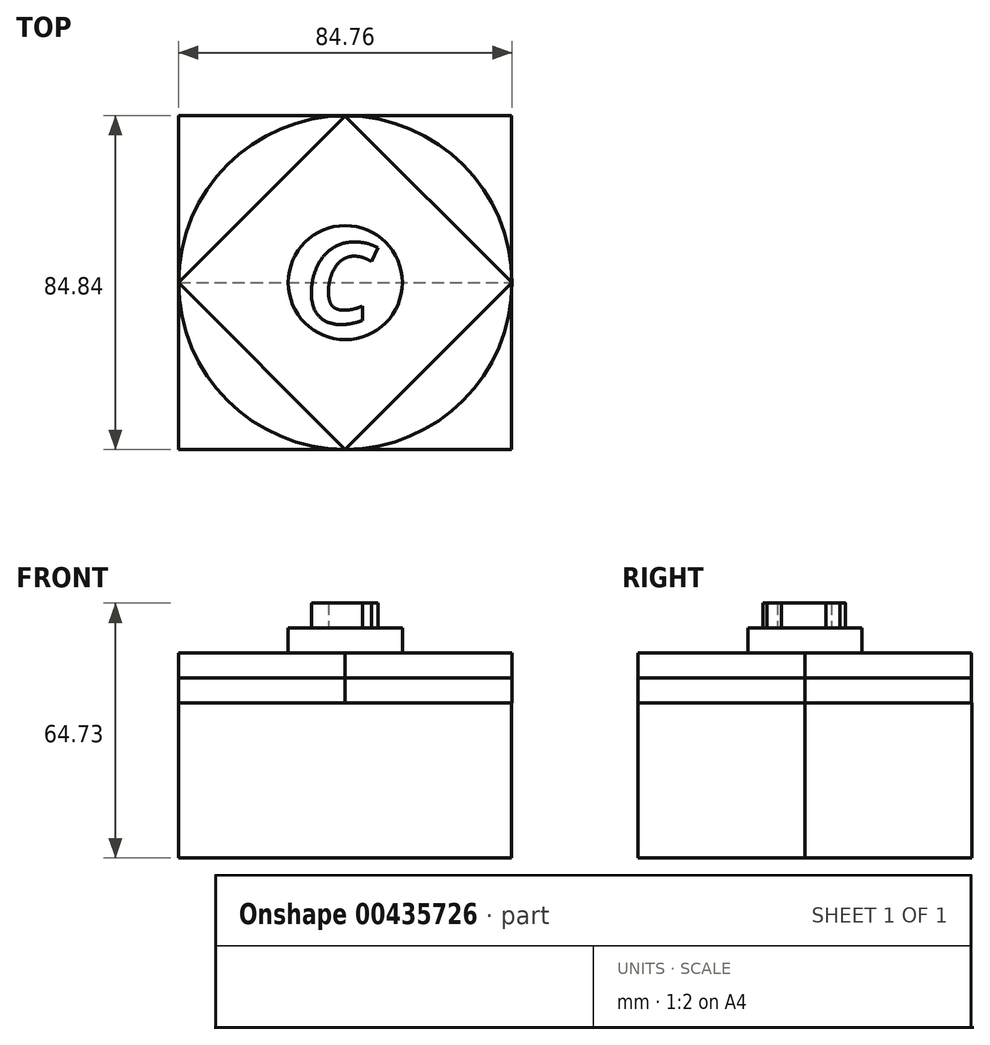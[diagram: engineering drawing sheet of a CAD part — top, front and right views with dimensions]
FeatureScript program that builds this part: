
annotation { "Feature Type Name" : "Feature", "Feature Type Description" : "" }
export const myFeature = defineFeature(function(context is Context, id is Id, definition is map)
    precondition{}
    {
        {
            var Q0;
            Q0=qCreatedBy(makeId("Top.planeOp"),FACE);
            var sketch = newSketch(context, id + "F0", { "sketchPlane" : qUnion([Q0])});
            skCircle(sketch, "E0", {"center": v(0, 0) * mm, "radius": 42.35 * mm});
            skLineSegment(sketch, "E1", {"start": v(0, 0) * mm, "end": v(0, 42.35) * mm});
            skLineSegment(sketch, "E2", {"start": v(0, 42.35) * mm, "end": v(-42.35, 0) * mm});
            skLineSegment(sketch, "E3", {"start": v(-42.35, 0) * mm, "end": v(0, -42.35) * mm});
            skLineSegment(sketch, "E4", {"start": v(0, -42.35) * mm, "end": v(42.35, 0) * mm});
            skLineSegment(sketch, "E5", {"start": v(42.35, 0) * mm, "end": v(0, 42.35) * mm});
            skLineSegment(sketch, "E6", {"start": v(0, 0) * mm, "end": v(42.35, 0) * mm});
            skLineSegment(sketch, "E7", {"start": v(0, 0) * mm, "end": v(0, -42.35) * mm});
            skLineSegment(sketch, "E8", {"start": v(0, 0) * mm, "end": v(-42.35, 0) * mm});
            skCircle(sketch, "E9", {"center": v(0, 0) * mm, "radius": 14.5 * mm});
            skText(sketch, "E10", { "text": "C", "fontName": "OpenSans-BoldItalic.ttf"});
            const initialGuessF0  = {"E10": [-0.01032, -0.01037, 1, 0, 0.02054]};
            skSetInitialGuess(sketch, initialGuessF0);
            skSolve(sketch);
        }
        {
            var Q0;
            {var subQ0=sQuery(id+"F0.wireOp",EDGE,"E2");Q0=makeQuery(id+"F0.imprint","IMPRINT",FACE,{"disambiguationData":[TD([[makeQuery(id+"F0.imprint","IMPRINT",EDGE,{"derivedFrom":subQ0}),-1.0]])]});}
            var Q1;
            {var subQ0=sQuery(id+"F0.wireOp",EDGE,"E5");Q1=makeQuery(id+"F0.imprint","IMPRINT",FACE,{"disambiguationData":[TD([[makeQuery(id+"F0.imprint","IMPRINT",EDGE,{"derivedFrom":subQ0}),-1.0]])]});}
            var Q2;
            {var subQ0=sQuery(id+"F0.wireOp",EDGE,"E4");Q2=makeQuery(id+"F0.imprint","IMPRINT",FACE,{"disambiguationData":[TD([[makeQuery(id+"F0.imprint","IMPRINT",EDGE,{"derivedFrom":subQ0}),-1.0]])]});}
            var Q3;
            {var subQ0=sQuery(id+"F0.wireOp",EDGE,"E3");Q3=makeQuery(id+"F0.imprint","IMPRINT",FACE,{"disambiguationData":[TD([[makeQuery(id+"F0.imprint","IMPRINT",EDGE,{"derivedFrom":subQ0}),-1.0]])]});}
            extrude(context, id + "F1", {"entities" : qUnion([Q0, Q1, Q2, Q3]), "depth" : 6.35 * mm});
        }
        {
            var Q0;
            {var subQ0=sQuery(id+"F0.wireOp",EDGE,"E2");Q0=makeQuery(id+"F0.imprint","IMPRINT",FACE,{"disambiguationData":[TD([[makeQuery(id+"F0.imprint","IMPRINT",EDGE,{"derivedFrom":subQ0}),1.0]])]});}
            var Q1;
            {var subQ0=sQuery(id+"F0.wireOp",EDGE,"E5");Q1=makeQuery(id+"F0.imprint","IMPRINT",FACE,{"disambiguationData":[TD([[makeQuery(id+"F0.imprint","IMPRINT",EDGE,{"derivedFrom":subQ0}),1.0]])]});}
            var Q2;
            {var subQ0=sQuery(id+"F0.wireOp",EDGE,"E4");Q2=makeQuery(id+"F0.imprint","IMPRINT",FACE,{"disambiguationData":[TD([[makeQuery(id+"F0.imprint","IMPRINT",EDGE,{"derivedFrom":subQ0}),1.0]])]});}
            var Q3;
            {var subQ0=sQuery(id+"F0.wireOp",EDGE,"E3");Q3=makeQuery(id+"F0.imprint","IMPRINT",FACE,{"disambiguationData":[TD([[makeQuery(id+"F0.imprint","IMPRINT",EDGE,{"derivedFrom":subQ0}),1.0]])]});}
            extrude(context, id + "F2", {"entities" : qUnion([Q0, Q1, Q2, Q3]), "depth" : 12.7 * mm});
        }
        {
            var Q0;
            {var subQ1=sQuery(id+"F0.wireOp",EDGE,"E1");var subQ3=sQuery(id+"F0.wireOp",EDGE,"E9");var subQ4=makeQuery(id+"F0.imprint","INTERSECT",VERTEX,{"derivedFrom":[subQ1,subQ3]});Q0=makeQuery(id+"F0.imprint","IMPRINT",FACE,{"disambiguationData":[TD([[makeQuery(id+"F0.imprint","IMPRINT",EDGE,{"disambiguationData":[TD([[subQ4,-1.0]])],"derivedFrom":subQ3}),1.0]])]});}
            var Q1;
            {var subQ1=sQuery(id+"F0.wireOp",EDGE,"E1");var subQ3=sQuery(id+"F0.wireOp",EDGE,"E9");var subQ4=makeQuery(id+"F0.imprint","INTERSECT",VERTEX,{"derivedFrom":[subQ1,subQ3]});Q1=makeQuery(id+"F0.imprint","IMPRINT",FACE,{"disambiguationData":[TD([[makeQuery(id+"F0.imprint","IMPRINT",EDGE,{"disambiguationData":[TD([[subQ4,1.0]])],"derivedFrom":subQ3}),1.0]])]});}
            var Q2;
            {var subQ1=sQuery(id+"F0.wireOp",EDGE,"E6");var subQ3=sQuery(id+"F0.wireOp",EDGE,"E9");var subQ4=makeQuery(id+"F0.imprint","INTERSECT",VERTEX,{"derivedFrom":[subQ1,subQ3]});Q2=makeQuery(id+"F0.imprint","IMPRINT",FACE,{"disambiguationData":[TD([[makeQuery(id+"F0.imprint","IMPRINT",EDGE,{"disambiguationData":[TD([[subQ4,1.0]])],"derivedFrom":subQ3}),1.0]])]});}
            var Q3;
            {var subQ1=sQuery(id+"F0.wireOp",EDGE,"E7");var subQ3=sQuery(id+"F0.wireOp",EDGE,"E9");var subQ4=makeQuery(id+"F0.imprint","INTERSECT",VERTEX,{"derivedFrom":[subQ1,subQ3]});Q3=makeQuery(id+"F0.imprint","IMPRINT",FACE,{"disambiguationData":[TD([[makeQuery(id+"F0.imprint","IMPRINT",EDGE,{"disambiguationData":[TD([[subQ4,1.0]])],"derivedFrom":subQ3}),1.0]])]});}
            extrude(context, id + "F3", {"entities" : qUnion([Q0, Q1, Q2, Q3]), "operationType" : NewBodyOperationType.ADD, "depth" : 19.05 * mm});
        }
        {
            var Q0;
            {var subQ0=sQuery(id+"F0.wireOp",EDGE,"E10.sketch_text.stroke-13");Q0=makeQuery(id+"F0.imprint","IMPRINT",FACE,{"disambiguationData":[TD([[makeQuery(id+"F0.imprint","IMPRINT",EDGE,{"derivedFrom":subQ0}),-1.0]])]});}
            var Q1;
            {var subQ0=sQuery(id+"F0.wireOp",EDGE,"E10.sketch_text.stroke-3");Q1=makeQuery(id+"F0.imprint","IMPRINT",FACE,{"disambiguationData":[TD([[makeQuery(id+"F0.imprint","IMPRINT",EDGE,{"derivedFrom":subQ0}),-1.0]])]});}
            var Q2;
            {var subQ0=sQuery(id+"F0.wireOp",EDGE,"E10.sketch_text.stroke-1");Q2=makeQuery(id+"F0.imprint","IMPRINT",FACE,{"disambiguationData":[TD([[makeQuery(id+"F0.imprint","IMPRINT",EDGE,{"derivedFrom":subQ0}),-1.0]])]});}
            var Q3;
            {var subQ5=sQuery(id+"F0.wireOp",EDGE,"E10.sketch_text.stroke-6");Q3=makeQuery(id+"F0.imprint","IMPRINT",FACE,{"disambiguationData":[TD([[makeQuery(id+"F0.imprint","IMPRINT",EDGE,{"derivedFrom":subQ5}),-1.0]])]});}
            extrude(context, id + "F4", {"entities" : qUnion([Q0, Q1, Q2, Q3]), "operationType" : NewBodyOperationType.ADD, "depth" : 25.4 * mm});
        }
        {
            var Q0;
            {var subQ0=sQuery(id+"F0.wireOp",EDGE,"E10.sketch_text.stroke-3");Q0=makeQuery(id+"F0.imprint","IMPRINT",FACE,{"disambiguationData":[TD([[makeQuery(id+"F0.imprint","IMPRINT",EDGE,{"derivedFrom":subQ0}),1.0]])]});}
            var Q1;
            {var subQ0=sQuery(id+"F0.wireOp",EDGE,"E10.sketch_text.stroke-1");Q1=makeQuery(id+"F0.imprint","IMPRINT",FACE,{"disambiguationData":[TD([[makeQuery(id+"F0.imprint","IMPRINT",EDGE,{"derivedFrom":subQ0}),1.0]])]});}
            extrude(context, id + "F5", {"entities" : qUnion([Q0, Q1]), "operationType" : NewBodyOperationType.ADD, "depth" : 19.05 * mm});
        }
        {
            var Q0;
            Q0=qCreatedBy(makeId("Front.planeOp"),FACE);
            var sketch = newSketch(context, id + "F6", { "sketchPlane" : qUnion([Q0])});
            skLineSegment(sketch, "E11.bottom", {"start": v(-42.41, 0) * mm, "end": v(42.22, 0) * mm});
            skLineSegment(sketch, "E11.top", {"start": v(-42.41, -39.33) * mm, "end": v(42.22, -39.33) * mm});
            skLineSegment(sketch, "E11.left", {"start": v(-42.41, -39.33) * mm, "end": v(-42.41, 0) * mm});
            skLineSegment(sketch, "E11.right", {"start": v(42.22, -39.33) * mm, "end": v(42.22, 0) * mm});
            skSolve(sketch);
        }
        {
            var Q0;
            Q0 = qSketchRegion(id + "F6", true);
            extrude(context, id + "F7", {"entities" : qUnion([Q0]), "depth" : -42.42 * mm});
        }
        {
            var Q0;
            Q0=makeQuery(id+"F7.opExtrude","CAP_FACE",FACE,{"disambiguationData":[OSD([sQuery(id+"F6.wireOp",EDGE,"E11.bottom"),sQuery(id+"F6.wireOp",EDGE,"E11.top"),sQuery(id+"F6.wireOp",EDGE,"E11.left"),sQuery(id+"F6.wireOp",EDGE,"E11.right")])],"isStart":true});
            extrude(context, id + "F8", {"entities" : qUnion([Q0]), "depth" : 42.42 * mm});
        }
    });
